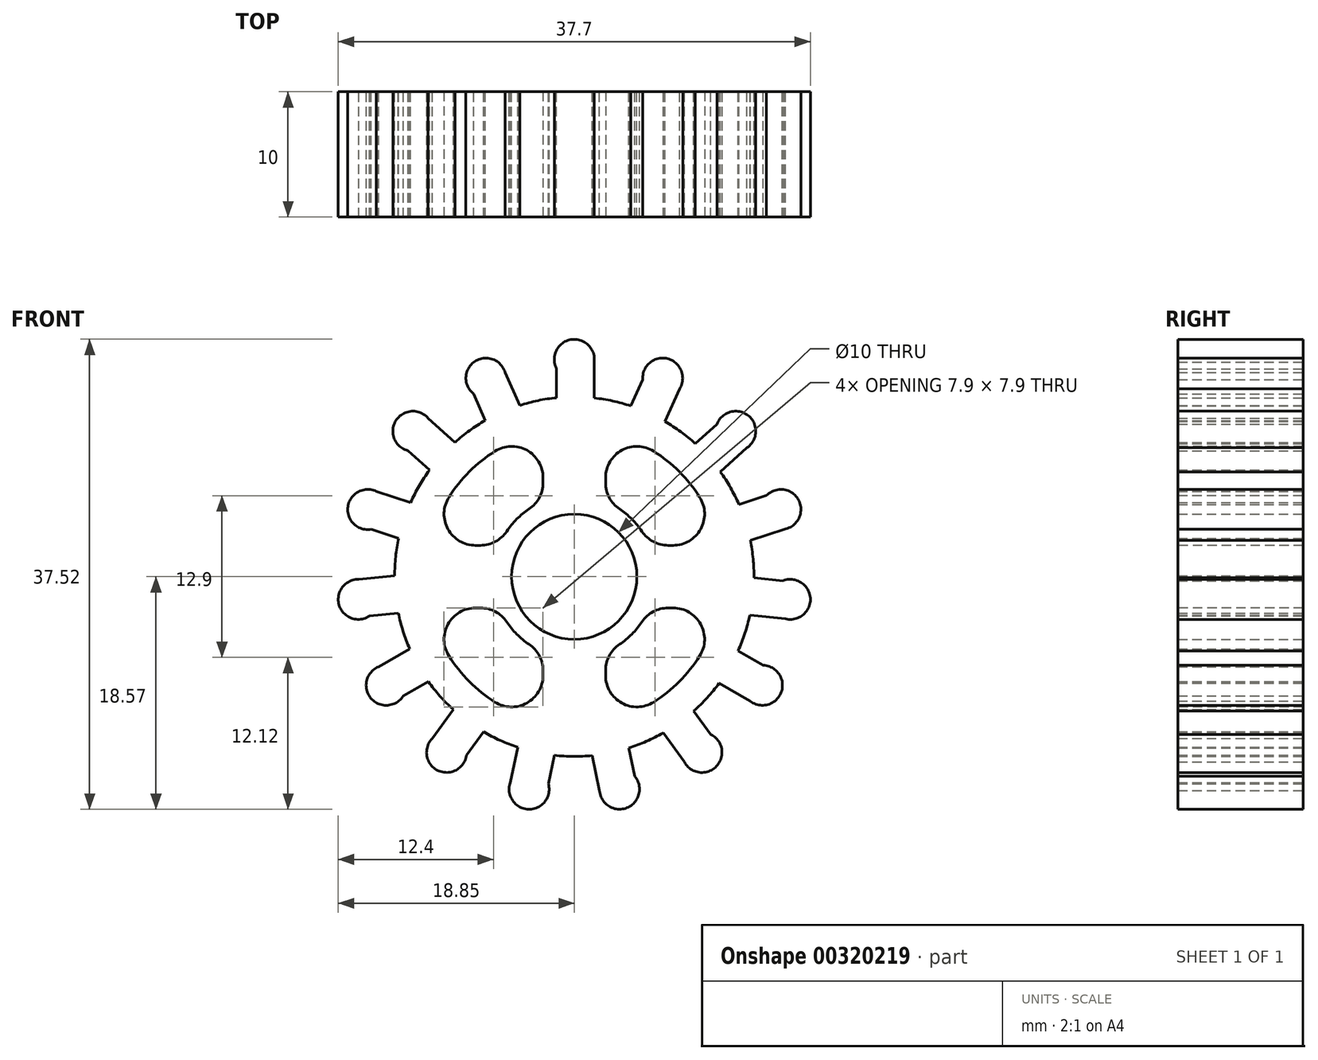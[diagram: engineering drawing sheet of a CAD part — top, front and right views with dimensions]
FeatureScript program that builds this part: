
annotation { "Feature Type Name" : "Feature", "Feature Type Description" : "" }
export const myFeature = defineFeature(function(context is Context, id is Id, definition is map)
    precondition{}
    {
        {
            var Q0;
            Q0=qCreatedBy(makeId("Front.planeOp"),FACE);
            var sketch = newSketch(context, id + "F0", { "sketchPlane" : qUnion([Q0])});
            skCircle(sketch, "E0", {"center": v(0, 0) * mm, "radius": 5 * mm});
            skArc(sketch, "E1", {"start": v(-7.1, 12.47) * mm, "mid": v(-8.37, 11.66) * mm, "end": v(-9.54, 10.72) * mm});
            skArc(sketch, "E2", {"start": v(1.59, 17.13) * mm, "mid": v(-0.28, 18.92) * mm, "end": v(-1.41, 16.6) * mm});
            skLineSegment(sketch, "E3", {"start": v(1.59, 17.13) * mm, "end": v(1.59, 14.26) * mm});
            skLineSegment(sketch, "E4", {"start": v(-1.41, 16.6) * mm, "end": v(-1.41, 14.28) * mm});
            skLineSegment(sketch, "E5.1.0", {"start": v(-5.52, 16.3) * mm, "end": v(-4.35, 13.67) * mm});
            skArc(sketch, "E5.1.1", {"start": v(-5.52, 16.3) * mm, "mid": v(-7.95, 17.17) * mm, "end": v(-8.04, 14.59) * mm});
            skLineSegment(sketch, "E5.1.2", {"start": v(-8.04, 14.59) * mm, "end": v(-7.1, 12.47) * mm});
            skLineSegment(sketch, "E5.2.0", {"start": v(-11.67, 12.64) * mm, "end": v(-9.54, 10.72) * mm});
            skArc(sketch, "E5.2.1", {"start": v(-11.67, 12.64) * mm, "mid": v(-14.25, 12.45) * mm, "end": v(-13.28, 10.05) * mm});
            skLineSegment(sketch, "E5.2.2", {"start": v(-13.28, 10.05) * mm, "end": v(-11.56, 8.5) * mm});
            skLineSegment(sketch, "E5.3.0", {"start": v(-15.8, 6.8) * mm, "end": v(-13.07, 5.92) * mm});
            skArc(sketch, "E5.3.1", {"start": v(-15.8, 6.8) * mm, "mid": v(-18.08, 5.58) * mm, "end": v(-16.22, 3.78) * mm});
            skLineSegment(sketch, "E5.3.2", {"start": v(-16.22, 3.78) * mm, "end": v(-14.02, 3.07) * mm});
            skLineSegment(sketch, "E5.4.0", {"start": v(-17.2, -0.21) * mm, "end": v(-14.35, 0.09) * mm});
            skArc(sketch, "E5.4.1", {"start": v(-17.2, -0.21) * mm, "mid": v(-18.79, -2.26) * mm, "end": v(-16.36, -3.14) * mm});
            skLineSegment(sketch, "E5.4.2", {"start": v(-16.36, -3.14) * mm, "end": v(-14.05, -2.9) * mm});
            skLineSegment(sketch, "E5.5.0", {"start": v(-15.63, -7.2) * mm, "end": v(-13.14, -5.76) * mm});
            skArc(sketch, "E5.5.1", {"start": v(-15.63, -7.2) * mm, "mid": v(-16.25, -9.7) * mm, "end": v(-13.67, -9.52) * mm});
            skLineSegment(sketch, "E5.5.2", {"start": v(-13.67, -9.52) * mm, "end": v(-11.66, -8.37) * mm});
            skLineSegment(sketch, "E5.6.0", {"start": v(-11.35, -12.93) * mm, "end": v(-9.67, -10.6) * mm});
            skArc(sketch, "E5.6.1", {"start": v(-11.35, -12.93) * mm, "mid": v(-10.9, -15.47) * mm, "end": v(-8.61, -14.26) * mm});
            skLineSegment(sketch, "E5.6.2", {"start": v(-8.61, -14.26) * mm, "end": v(-7.25, -12.38) * mm});
            skLineSegment(sketch, "E5.7.0", {"start": v(-5.11, -16.43) * mm, "end": v(-4.52, -13.62) * mm});
            skArc(sketch, "E5.7.1", {"start": v(-5.11, -16.43) * mm, "mid": v(-3.66, -18.57) * mm, "end": v(-2.07, -16.53) * mm});
            skLineSegment(sketch, "E5.7.2", {"start": v(-2.07, -16.53) * mm, "end": v(-1.59, -14.26) * mm});
            skLineSegment(sketch, "E5.8.0", {"start": v(2.01, -17.08) * mm, "end": v(1.41, -14.28) * mm});
            skArc(sketch, "E5.8.1", {"start": v(2.01, -17.08) * mm, "mid": v(4.2, -18.45) * mm, "end": v(4.83, -15.94) * mm});
            skLineSegment(sketch, "E5.8.2", {"start": v(4.83, -15.94) * mm, "end": v(4.35, -13.67) * mm});
            skLineSegment(sketch, "E5.9.0", {"start": v(8.79, -14.79) * mm, "end": v(7.1, -12.47) * mm});
            skArc(sketch, "E5.9.1", {"start": v(8.79, -14.79) * mm, "mid": v(11.35, -15.14) * mm, "end": v(10.9, -12.6) * mm});
            skLineSegment(sketch, "E5.9.2", {"start": v(10.9, -12.6) * mm, "end": v(9.54, -10.72) * mm});
            skLineSegment(sketch, "E5.10.0", {"start": v(14.04, -9.94) * mm, "end": v(11.56, -8.5) * mm});
            skArc(sketch, "E5.10.1", {"start": v(14.04, -9.94) * mm, "mid": v(16.53, -9.22) * mm, "end": v(15.08, -7.07) * mm});
            skLineSegment(sketch, "E5.10.2", {"start": v(15.08, -7.07) * mm, "end": v(13.07, -5.91) * mm});
            skLineSegment(sketch, "E5.11.0", {"start": v(16.87, -3.37) * mm, "end": v(14.02, -3.07) * mm});
            skArc(sketch, "E5.11.1", {"start": v(16.87, -3.37) * mm, "mid": v(18.85, -1.7) * mm, "end": v(16.65, -0.33) * mm});
            skLineSegment(sketch, "E5.11.2", {"start": v(16.65, -0.33) * mm, "end": v(14.35, -0.09) * mm});
            skLineSegment(sketch, "E5.12.0", {"start": v(16.78, 3.79) * mm, "end": v(14.05, 2.9) * mm});
            skArc(sketch, "E5.12.1", {"start": v(16.78, 3.79) * mm, "mid": v(17.9, 6.11) * mm, "end": v(15.35, 6.47) * mm});
            skLineSegment(sketch, "E5.12.2", {"start": v(15.35, 6.47) * mm, "end": v(13.14, 5.76) * mm});
            skLineSegment(sketch, "E5.13.0", {"start": v(13.8, 10.28) * mm, "end": v(11.66, 8.37) * mm});
            skArc(sketch, "E5.13.1", {"start": v(13.8, 10.28) * mm, "mid": v(13.87, 12.87) * mm, "end": v(11.39, 12.16) * mm});
            skLineSegment(sketch, "E5.13.2", {"start": v(11.39, 12.16) * mm, "end": v(9.67, 10.6) * mm});
            skLineSegment(sketch, "E5.14.0", {"start": v(8.42, 15) * mm, "end": v(7.25, 12.38) * mm});
            skArc(sketch, "E5.14.1", {"start": v(8.42, 15) * mm, "mid": v(7.44, 17.4) * mm, "end": v(5.46, 15.74) * mm});
            skLineSegment(sketch, "E5.14.2", {"start": v(5.46, 15.74) * mm, "end": v(4.52, 13.62) * mm});
            skArc(sketch, "E6.trimOffspring", {"start": v(-11.56, 8.5) * mm, "mid": v(-12.38, 7.25) * mm, "end": v(-13.07, 5.92) * mm});
            skArc(sketch, "E7.trimOffspring", {"start": v(-14.02, 3.07) * mm, "mid": v(-14.26, 1.59) * mm, "end": v(-14.35, 0.09) * mm});
            skArc(sketch, "E8.trimOffspring", {"start": v(-14.05, -2.9) * mm, "mid": v(-13.67, -4.35) * mm, "end": v(-13.14, -5.76) * mm});
            skArc(sketch, "E9.trimOffspring", {"start": v(-11.66, -8.37) * mm, "mid": v(-10.72, -9.54) * mm, "end": v(-9.67, -10.6) * mm});
            skArc(sketch, "E10.trimOffspring", {"start": v(-7.25, -12.38) * mm, "mid": v(-5.92, -13.07) * mm, "end": v(-4.52, -13.62) * mm});
            skArc(sketch, "E11.trimOffspring", {"start": v(-1.59, -14.26) * mm, "mid": v(-0.09, -14.35) * mm, "end": v(1.41, -14.28) * mm});
            skArc(sketch, "E12.trimOffspring", {"start": v(4.35, -13.67) * mm, "mid": v(5.76, -13.14) * mm, "end": v(7.1, -12.47) * mm});
            skArc(sketch, "E13.trimOffspring", {"start": v(9.54, -10.72) * mm, "mid": v(10.6, -9.67) * mm, "end": v(11.56, -8.5) * mm});
            skArc(sketch, "E14.trimOffspring", {"start": v(13.07, -5.91) * mm, "mid": v(13.62, -4.52) * mm, "end": v(14.02, -3.07) * mm});
            skArc(sketch, "E15.trimOffspring", {"start": v(14.35, -0.09) * mm, "mid": v(14.28, 1.41) * mm, "end": v(14.05, 2.9) * mm});
            skArc(sketch, "E16.trimOffspring", {"start": v(13.14, 5.76) * mm, "mid": v(12.47, 7.1) * mm, "end": v(11.66, 8.37) * mm});
            skArc(sketch, "E17.trimOffspring", {"start": v(9.67, 10.6) * mm, "mid": v(8.5, 11.56) * mm, "end": v(7.25, 12.38) * mm});
            skArc(sketch, "E18.trimOffspring", {"start": v(4.52, 13.62) * mm, "mid": v(3.07, 14.02) * mm, "end": v(1.59, 14.26) * mm});
            skArc(sketch, "E19.trimOffspring", {"start": v(-1.41, 14.28) * mm, "mid": v(-2.9, 14.05) * mm, "end": v(-4.35, 13.67) * mm});
            skSolve(sketch);
        }
        {
            var Q0;
            Q0=qSketchRegion(id+"F0",true);
            extrude(context, id + "F1", {"entities" : qUnion([Q0]), "endBound" : BoundingType.SYMMETRIC, "depth" : 10 * mm});
        }
        {
            var Q0;
            Q0=makeQuery(id+"F1.opExtrude","CAP_FACE",FACE,{"disambiguationData":[OSD([sQuery(id+"F0.wireOp",EDGE,"E0"),sQuery(id+"F0.wireOp",EDGE,"E1"),sQuery(id+"F0.wireOp",EDGE,"E2"),sQuery(id+"F0.wireOp",EDGE,"E3"),sQuery(id+"F0.wireOp",EDGE,"E4"),sQuery(id+"F0.wireOp",EDGE,"E5.1.0"),sQuery(id+"F0.wireOp",EDGE,"E5.1.1"),sQuery(id+"F0.wireOp",EDGE,"E5.1.2"),sQuery(id+"F0.wireOp",EDGE,"E5.2.0"),sQuery(id+"F0.wireOp",EDGE,"E5.2.1"),sQuery(id+"F0.wireOp",EDGE,"E5.2.2"),sQuery(id+"F0.wireOp",EDGE,"E5.3.0"),sQuery(id+"F0.wireOp",EDGE,"E5.3.1"),sQuery(id+"F0.wireOp",EDGE,"E5.3.2"),sQuery(id+"F0.wireOp",EDGE,"E5.4.0"),sQuery(id+"F0.wireOp",EDGE,"E5.4.1"),sQuery(id+"F0.wireOp",EDGE,"E5.4.2"),sQuery(id+"F0.wireOp",EDGE,"E5.5.0"),sQuery(id+"F0.wireOp",EDGE,"E5.5.1"),sQuery(id+"F0.wireOp",EDGE,"E5.5.2"),sQuery(id+"F0.wireOp",EDGE,"E5.6.0"),sQuery(id+"F0.wireOp",EDGE,"E5.6.1"),sQuery(id+"F0.wireOp",EDGE,"E5.6.2"),sQuery(id+"F0.wireOp",EDGE,"E5.7.0"),sQuery(id+"F0.wireOp",EDGE,"E5.7.1"),sQuery(id+"F0.wireOp",EDGE,"E5.7.2"),sQuery(id+"F0.wireOp",EDGE,"E5.8.0"),sQuery(id+"F0.wireOp",EDGE,"E5.8.1"),sQuery(id+"F0.wireOp",EDGE,"E5.8.2"),sQuery(id+"F0.wireOp",EDGE,"E5.9.0"),sQuery(id+"F0.wireOp",EDGE,"E5.9.1"),sQuery(id+"F0.wireOp",EDGE,"E5.9.2"),sQuery(id+"F0.wireOp",EDGE,"E5.10.0"),sQuery(id+"F0.wireOp",EDGE,"E5.10.1"),sQuery(id+"F0.wireOp",EDGE,"E5.10.2"),sQuery(id+"F0.wireOp",EDGE,"E5.11.0"),sQuery(id+"F0.wireOp",EDGE,"E5.11.1"),sQuery(id+"F0.wireOp",EDGE,"E5.11.2"),sQuery(id+"F0.wireOp",EDGE,"E5.12.0"),sQuery(id+"F0.wireOp",EDGE,"E5.12.1"),sQuery(id+"F0.wireOp",EDGE,"E5.12.2"),sQuery(id+"F0.wireOp",EDGE,"E5.13.0"),sQuery(id+"F0.wireOp",EDGE,"E5.13.1"),sQuery(id+"F0.wireOp",EDGE,"E5.13.2"),sQuery(id+"F0.wireOp",EDGE,"E5.14.0"),sQuery(id+"F0.wireOp",EDGE,"E5.14.1"),sQuery(id+"F0.wireOp",EDGE,"E5.14.2"),sQuery(id+"F0.wireOp",EDGE,"E6.trimOffspring"),sQuery(id+"F0.wireOp",EDGE,"E7.trimOffspring"),sQuery(id+"F0.wireOp",EDGE,"E8.trimOffspring"),sQuery(id+"F0.wireOp",EDGE,"E9.trimOffspring"),sQuery(id+"F0.wireOp",EDGE,"E10.trimOffspring"),sQuery(id+"F0.wireOp",EDGE,"E11.trimOffspring"),sQuery(id+"F0.wireOp",EDGE,"E12.trimOffspring"),sQuery(id+"F0.wireOp",EDGE,"E13.trimOffspring"),sQuery(id+"F0.wireOp",EDGE,"E14.trimOffspring"),sQuery(id+"F0.wireOp",EDGE,"E15.trimOffspring"),sQuery(id+"F0.wireOp",EDGE,"E16.trimOffspring"),sQuery(id+"F0.wireOp",EDGE,"E17.trimOffspring"),sQuery(id+"F0.wireOp",EDGE,"E18.trimOffspring"),sQuery(id+"F0.wireOp",EDGE,"E19.trimOffspring")])],"isStart":false});
            var sketch = newSketch(context, id + "F2", { "sketchPlane" : qUnion([Q0])});
            skArc(sketch, "E20", {"start": v(-10.01, 6.34) * mm, "mid": v(-8.38, 8.38) * mm, "end": v(-6.34, 10.01) * mm});
            skLineSegment(sketch, "E21", {"start": v(0, 0) * mm, "end": v(0, 23.63) * mm, "construction": true});
            skLineSegment(sketch, "E22", {"start": v(0, 23.63) * mm, "end": v(0, 11.85) * mm, "construction": true});
            skLineSegment(sketch, "E23", {"start": v(0, 0) * mm, "end": v(-36.4, 0) * mm, "construction": true});
            skLineSegment(sketch, "E24", {"start": v(-2.5, 7.9) * mm, "end": v(-2.5, 7.48) * mm});
            skLineSegment(sketch, "E25", {"start": v(-7.9, 2.5) * mm, "end": v(-7.48, 2.5) * mm});
            skArc(sketch, "E26.trimOffspring", {"start": v(-3.61, 5.4) * mm, "mid": v(-4.6, 4.6) * mm, "end": v(-5.4, 3.61) * mm});
            skPoint(sketch, "E27.orphan", {"position": v(0, 11.85) * mm});
            skPoint(sketch, "E28.orphan", {"position": v(-11.85, 0) * mm});
            skPoint(sketch, "E29.visualSharp", {"position": v(-2.5, 11.58) * mm});
            skArc(sketch, "E29.filletArc", {"start": v(-2.5, 7.9) * mm, "mid": v(-3.8, 10.1) * mm, "end": v(-6.34, 10.01) * mm});
            skPoint(sketch, "E30.visualSharp", {"position": v(-11.58, 2.5) * mm});
            skArc(sketch, "E30.filletArc", {"start": v(-10.01, 6.34) * mm, "mid": v(-10.1, 3.8) * mm, "end": v(-7.9, 2.5) * mm});
            skPoint(sketch, "E31.visualSharp", {"position": v(-6, 2.5) * mm});
            skArc(sketch, "E31.filletArc", {"start": v(-7.48, 2.5) * mm, "mid": v(-6.3, 2.8) * mm, "end": v(-5.4, 3.61) * mm});
            skPoint(sketch, "E32.visualSharp", {"position": v(-2.5, 6) * mm});
            skArc(sketch, "E32.filletArc", {"start": v(-3.61, 5.4) * mm, "mid": v(-2.8, 6.3) * mm, "end": v(-2.5, 7.48) * mm});
            skArc(sketch, "E33.MirrorCS", {"start": v(2.5, 7.9) * mm, "mid": v(3.8, 10.1) * mm, "end": v(6.34, 10.01) * mm});
            skArc(sketch, "E34.MirrorCS", {"start": v(10.01, 6.34) * mm, "mid": v(8.38, 8.38) * mm, "end": v(6.34, 10.01) * mm});
            skArc(sketch, "E35.MirrorCS", {"start": v(10.01, 6.34) * mm, "mid": v(10.1, 3.8) * mm, "end": v(7.9, 2.5) * mm});
            skLineSegment(sketch, "E36.MirrorCS", {"start": v(7.9, 2.5) * mm, "end": v(7.48, 2.5) * mm});
            skArc(sketch, "E37.MirrorCS", {"start": v(7.48, 2.5) * mm, "mid": v(6.3, 2.8) * mm, "end": v(5.4, 3.61) * mm});
            skArc(sketch, "E38.MirrorCS", {"start": v(3.61, 5.4) * mm, "mid": v(4.6, 4.6) * mm, "end": v(5.4, 3.61) * mm});
            skArc(sketch, "E39.MirrorCS", {"start": v(3.61, 5.4) * mm, "mid": v(2.8, 6.3) * mm, "end": v(2.5, 7.48) * mm});
            skLineSegment(sketch, "E40.MirrorCS", {"start": v(2.5, 7.9) * mm, "end": v(2.5, 7.48) * mm});
            skLineSegment(sketch, "E41.0", {"start": v(0, 5) * mm, "end": v(-10.4, 5) * mm});
            skLineSegment(sketch, "E42.MirrorCS", {"start": v(-7.9, -2.5) * mm, "end": v(-7.48, -2.5) * mm});
            skArc(sketch, "E43.MirrorCS", {"start": v(-10.01, -6.34) * mm, "mid": v(-10.1, -3.8) * mm, "end": v(-7.9, -2.5) * mm});
            skArc(sketch, "E44.MirrorCS", {"start": v(-10.01, -6.34) * mm, "mid": v(-8.38, -8.38) * mm, "end": v(-6.34, -10.01) * mm});
            skArc(sketch, "E45.MirrorCS", {"start": v(-2.5, -7.9) * mm, "mid": v(-3.8, -10.1) * mm, "end": v(-6.34, -10.01) * mm});
            skLineSegment(sketch, "E46.MirrorCS", {"start": v(-2.5, -7.9) * mm, "end": v(-2.5, -7.48) * mm});
            skPoint(sketch, "E47.MirrorP", {"position": v(-2.5, -6) * mm});
            skArc(sketch, "E48.MirrorCS", {"start": v(-3.61, -5.4) * mm, "mid": v(-4.6, -4.6) * mm, "end": v(-5.4, -3.61) * mm});
            skArc(sketch, "E49.MirrorCS", {"start": v(-3.61, -5.4) * mm, "mid": v(-2.8, -6.3) * mm, "end": v(-2.5, -7.48) * mm});
            skArc(sketch, "E50.MirrorCS", {"start": v(-7.48, -2.5) * mm, "mid": v(-6.3, -2.8) * mm, "end": v(-5.4, -3.61) * mm});
            skArc(sketch, "E51.MirrorCS", {"start": v(3.61, -5.4) * mm, "mid": v(2.8, -6.3) * mm, "end": v(2.5, -7.48) * mm});
            skLineSegment(sketch, "E52.MirrorCS", {"start": v(2.5, -7.9) * mm, "end": v(2.5, -7.48) * mm});
            skArc(sketch, "E53.MirrorCS", {"start": v(2.5, -7.9) * mm, "mid": v(3.8, -10.1) * mm, "end": v(6.34, -10.01) * mm});
            skArc(sketch, "E54.MirrorCS", {"start": v(10.01, -6.34) * mm, "mid": v(8.38, -8.38) * mm, "end": v(6.34, -10.01) * mm});
            skArc(sketch, "E55.MirrorCS", {"start": v(10.01, -6.34) * mm, "mid": v(10.1, -3.8) * mm, "end": v(7.9, -2.5) * mm});
            skLineSegment(sketch, "E56.MirrorCS", {"start": v(7.9, -2.5) * mm, "end": v(7.48, -2.5) * mm});
            skArc(sketch, "E57.MirrorCS", {"start": v(7.48, -2.5) * mm, "mid": v(6.3, -2.8) * mm, "end": v(5.4, -3.61) * mm});
            skArc(sketch, "E58.MirrorCS", {"start": v(3.61, -5.4) * mm, "mid": v(4.6, -4.6) * mm, "end": v(5.4, -3.61) * mm});
            skLineSegment(sketch, "E59.trimOffspring", {"start": v(0, 5) * mm, "end": v(0, 0) * mm, "construction": true});
            skSolve(sketch);
        }
        {
            var Q0;
            Q0=qSketchRegion(id+"F2",true);
            extrude(context, id + "F3", {"entities" : qUnion([Q0]), "operationType" : NewBodyOperationType.REMOVE, "oppositeDirection" : true, "depth" : 10 * mm});
        }
    });
